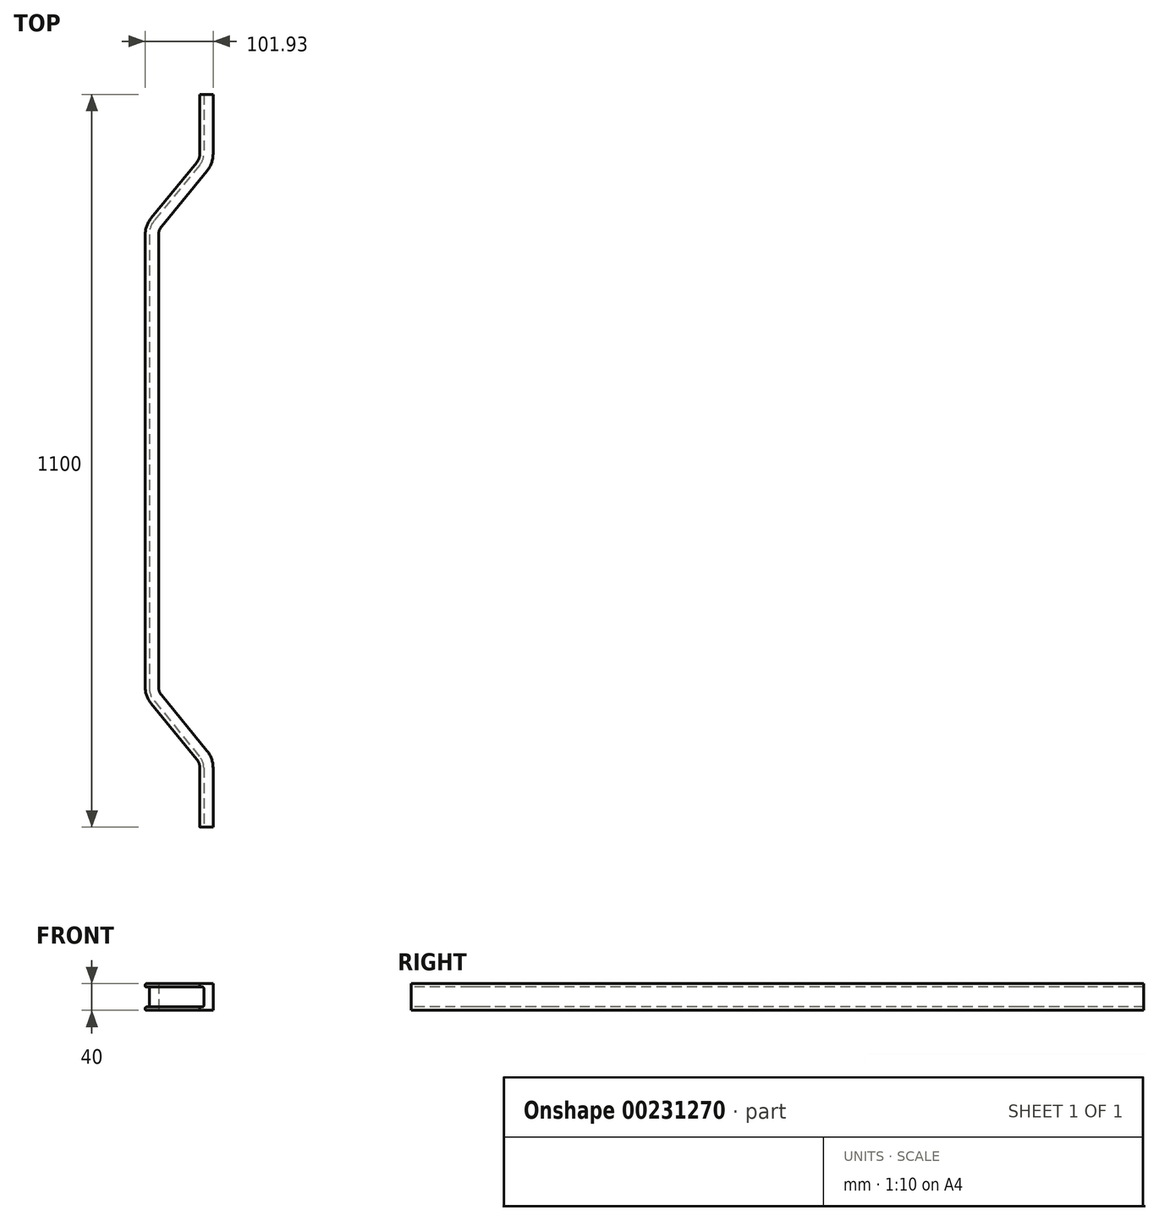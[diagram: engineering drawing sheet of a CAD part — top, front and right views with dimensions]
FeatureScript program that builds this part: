
annotation { "Feature Type Name" : "Feature", "Feature Type Description" : "" }
export const myFeature = defineFeature(function(context is Context, id is Id, definition is map)
    precondition{}
    {
        {
            var Q0;
            Q0=qCreatedBy(makeId("Front.planeOp"),FACE);
            var sketch = newSketch(context, id + "F0", { "sketchPlane" : qUnion([Q0])});
            skLineSegment(sketch, "E0.bottom", {"start": v(-8, 20) * mm, "end": v(10, 20) * mm});
            skLineSegment(sketch, "E0.top", {"start": v(-8, -20) * mm, "end": v(10, -20) * mm});
            skLineSegment(sketch, "E0.left", {"start": v(-10, 18) * mm, "end": v(-10, 17) * mm});
            skLineSegment(sketch, "E0.right", {"start": v(10, 20) * mm, "end": v(10, -20) * mm});
            skPoint(sketch, "E0.middle", {"position": v(0, 0) * mm});
            skLineSegment(sketch, "E1", {"start": v(-8, 15) * mm, "end": v(-6, 15) * mm});
            skLineSegment(sketch, "E2", {"start": v(-4, 13) * mm, "end": v(-4, -13) * mm});
            skLineSegment(sketch, "E3", {"start": v(-6, -15) * mm, "end": v(-8, -15) * mm});
            skLineSegment(sketch, "E4.trimOffspring", {"start": v(-10, -17) * mm, "end": v(-10, -18) * mm});
            skPoint(sketch, "E5.visualSharp", {"position": v(-10, 15) * mm});
            skArc(sketch, "E5.filletArc", {"start": v(-10, 17) * mm, "mid": v(-9.41, 15.59) * mm, "end": v(-8, 15) * mm});
            skPoint(sketch, "E6.visualSharp", {"position": v(-10, -15) * mm});
            skArc(sketch, "E6.filletArc", {"start": v(-8, -15) * mm, "mid": v(-9.41, -15.59) * mm, "end": v(-10, -17) * mm});
            skPoint(sketch, "E7.visualSharp", {"position": v(-10, 20) * mm});
            skArc(sketch, "E7.filletArc", {"start": v(-8, 20) * mm, "mid": v(-9.41, 19.41) * mm, "end": v(-10, 18) * mm});
            skPoint(sketch, "E8.visualSharp", {"position": v(-10, -20) * mm});
            skArc(sketch, "E8.filletArc", {"start": v(-10, -18) * mm, "mid": v(-9.41, -19.41) * mm, "end": v(-8, -20) * mm});
            skPoint(sketch, "E9.visualSharp", {"position": v(-4, 15) * mm});
            skArc(sketch, "E9.filletArc", {"start": v(-4, 13) * mm, "mid": v(-4.59, 14.41) * mm, "end": v(-6, 15) * mm});
            skPoint(sketch, "E10.visualSharp", {"position": v(-4, -15) * mm});
            skArc(sketch, "E10.filletArc", {"start": v(-6, -15) * mm, "mid": v(-4.59, -14.41) * mm, "end": v(-4, -13) * mm});
            skSolve(sketch);
        }
        {
            var Q0;
            Q0=qCreatedBy(makeId("Top.planeOp"),FACE);
            var sketch = newSketch(context, id + "F1", { "sketchPlane" : qUnion([Q0])});
            skLineSegment(sketch, "E11", {"start": v(0, 0) * mm, "end": v(0, -89.28) * mm});
            skLineSegment(sketch, "E12", {"start": v(-6.8, -108.3) * mm, "end": v(-75.13, -191.7) * mm});
            skLineSegment(sketch, "E13", {"start": v(-81.93, -210.72) * mm, "end": v(-81.93, -550) * mm});
            skLineSegment(sketch, "E14", {"start": v(-81.93, -550) * mm, "end": v(130.18, -550) * mm, "construction": true});
            skLineSegment(sketch, "E15.MirrorCS", {"start": v(0, -1100) * mm, "end": v(0, -1010.72) * mm});
            skLineSegment(sketch, "E16.MirrorCS", {"start": v(-6.8, -991.7) * mm, "end": v(-75.13, -908.3) * mm});
            skLineSegment(sketch, "E17.MirrorCS", {"start": v(-81.93, -889.28) * mm, "end": v(-81.93, -550) * mm});
            skPoint(sketch, "E18.visualSharp", {"position": v(0, -100) * mm});
            skArc(sketch, "E18.filletArc", {"start": v(-6.8, -108.3) * mm, "mid": v(-1.75, -99.37) * mm, "end": v(0, -89.28) * mm});
            skPoint(sketch, "E19.visualSharp", {"position": v(-81.93, -200) * mm});
            skArc(sketch, "E19.filletArc", {"start": v(-75.13, -191.7) * mm, "mid": v(-80.18, -200.63) * mm, "end": v(-81.93, -210.72) * mm});
            skPoint(sketch, "E20.visualSharp", {"position": v(-81.93, -900) * mm});
            skArc(sketch, "E20.filletArc", {"start": v(-81.93, -889.28) * mm, "mid": v(-80.18, -899.37) * mm, "end": v(-75.13, -908.3) * mm});
            skPoint(sketch, "E21.visualSharp", {"position": v(0, -1000) * mm});
            skArc(sketch, "E21.filletArc", {"start": v(0, -1010.72) * mm, "mid": v(-1.75, -1000.63) * mm, "end": v(-6.8, -991.7) * mm});
            skSolve(sketch);
        }
        {
            var Q0;
            Q0=makeQuery(id+"F0.imprint","IMPRINT",FACE,{"disambiguationData":[TD([[makeQuery(id+"F0.imprint","IMPRINT",EDGE,{"derivedFrom":sQuery(id+"F0.wireOp",EDGE,"E0.bottom")}),-1.0]])]});
            var Q1;
            Q1=sQuery(id+"F1.wireOp",EDGE,"E11");
            var Q2;
            Q2=sQuery(id+"F1.wireOp",EDGE,"E18.filletArc");
            var Q3;
            Q3=sQuery(id+"F1.wireOp",EDGE,"E12");
            var Q4;
            Q4=sQuery(id+"F1.wireOp",EDGE,"E13");
            var Q5;
            Q5=sQuery(id+"F1.wireOp",EDGE,"E19.filletArc");
            var Q6;
            Q6=sQuery(id+"F1.wireOp",EDGE,"E17.MirrorCS");
            var Q7;
            Q7=sQuery(id+"F1.wireOp",EDGE,"E20.filletArc");
            var Q8;
            Q8=sQuery(id+"F1.wireOp",EDGE,"E16.MirrorCS");
            var Q9;
            Q9=sQuery(id+"F1.wireOp",EDGE,"E21.filletArc");
            var Q10;
            Q10=sQuery(id+"F1.wireOp",EDGE,"E15.MirrorCS");
            sweep(context, id + "F2", {"profiles" : qUnion([Q0]), "path" : qUnion([Q1, Q2, Q3, Q4, Q5, Q6, Q7, Q8, Q9, Q10])});
        }
    });
